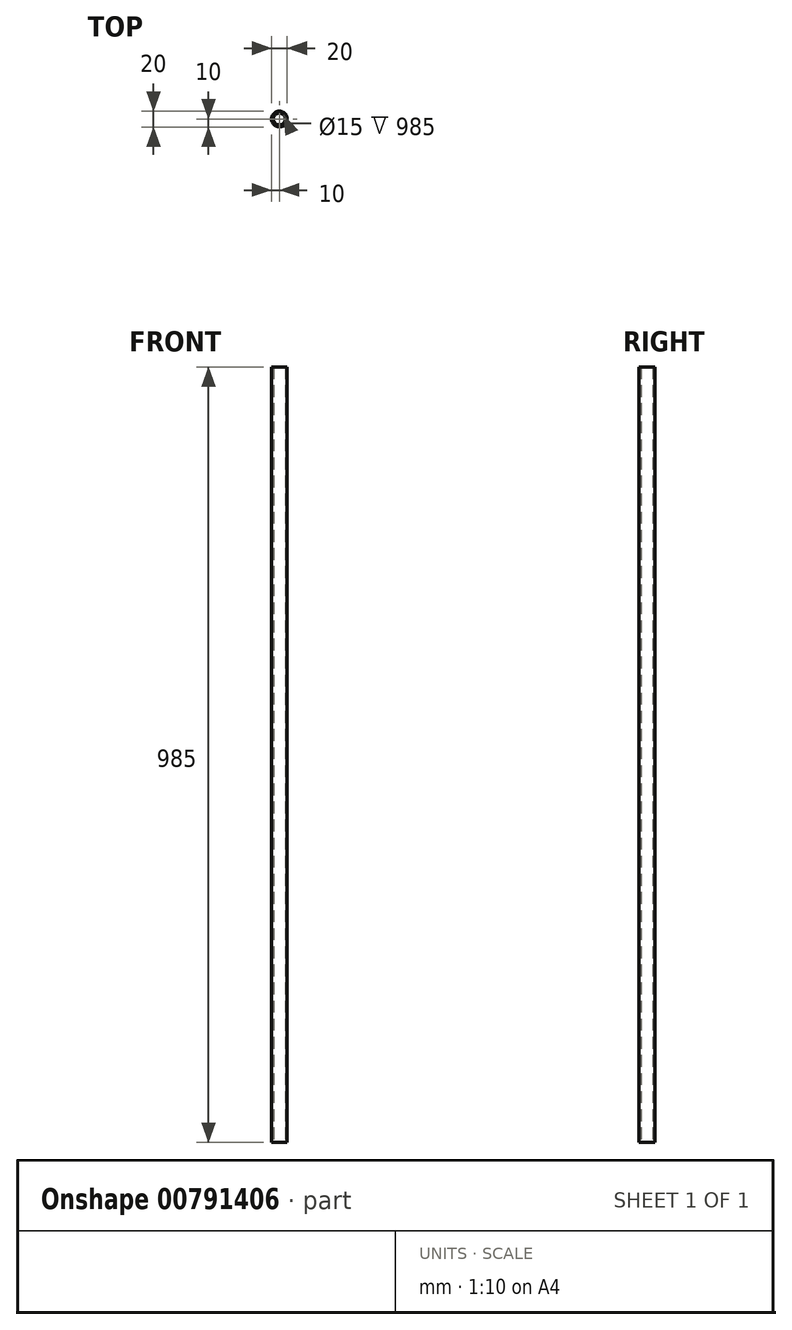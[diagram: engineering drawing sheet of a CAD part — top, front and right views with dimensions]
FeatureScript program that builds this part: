
annotation { "Feature Type Name" : "Feature", "Feature Type Description" : "" }
export const myFeature = defineFeature(function(context is Context, id is Id, definition is map)
    precondition{}
    {
        {
            var Q0;
            Q0=qCreatedBy(makeId("Top.planeOp"),FACE);
            var sketch = newSketch(context, id + "F0", { "sketchPlane" : qUnion([Q0])});
            skCircle(sketch, "E0", {"center": v(0, 0) * mm, "radius": 10 * mm});
            skCircle(sketch, "E1", {"center": v(0, 0) * mm, "radius": 7.5 * mm});
            skCircle(sketch, "E2", {"center": v(149.2, -44.9) * mm, "radius": 10 * mm});
            skCircle(sketch, "E3", {"center": v(149.2, -44.9) * mm, "radius": 7.5 * mm});
            skSolve(sketch);
        }
        {
            var Q0;
            Q0=makeQuery(id+"F0.imprint","IMPRINT",FACE,{"disambiguationData":[TD([[makeQuery(id+"F0.imprint","IMPRINT",EDGE,{"derivedFrom":sQuery(id+"F0.wireOp",EDGE,"E0")}),1.0]])]});
            extrude(context, id + "F1", {"entities" : qUnion([Q0]), "depth" : 985 * mm, "offsetDistance" : 25 * mm});
        }
        {
            var Q0;
            Q0=qCreatedBy(makeId("Right.planeOp"),FACE);
            var sketch = newSketch(context, id + "F2", { "sketchPlane" : qUnion([Q0])});
            skLineSegment(sketch, "E4", {"start": v(-97.42, 1122.5) * mm, "end": v(267.58, 1122.5) * mm});
            skLineSegment(sketch, "E5", {"start": v(267.58, 1122.5) * mm, "end": v(-97.42, 927.5) * mm});
            skLineSegment(sketch, "E6", {"start": v(-97.42, 927.5) * mm, "end": v(-97.42, 1122.5) * mm});
            skSolve(sketch);
        }
        {
            var Q0;
            Q0=makeQuery(id+"F0.imprint","IMPRINT",FACE,{"disambiguationData":[TD([[makeQuery(id+"F0.imprint","IMPRINT",EDGE,{"derivedFrom":sQuery(id+"F0.wireOp",EDGE,"E2")}),1.0]])]});
            var Q1;
            Q1=sQuery(id+"F0.wireOp",EDGE,"E3");
            var Q2;
            Q2=sQuery(id+"F0.wireOp",EDGE,"E2");
            extrude(context, id + "F3", {"entities" : qUnion([Q0]), "surfaceEntities" : qUnion([Q1, Q2]), "depth" : 1005 * mm, "offsetDistance" : 25 * mm});
        }
        {
            var Q0;
            Q0=makeQuery(id+"F3.opExtrude","SWEPT_BODY",BODY,{"disambiguationData":[OSD([sQuery(id+"F0.wireOp",EDGE,"E2"),sQuery(id+"F0.wireOp",EDGE,"E3")])]});
            deleteBodies(context, id + "F4", {"entities" : qUnion([Q0])});
        }
    });
